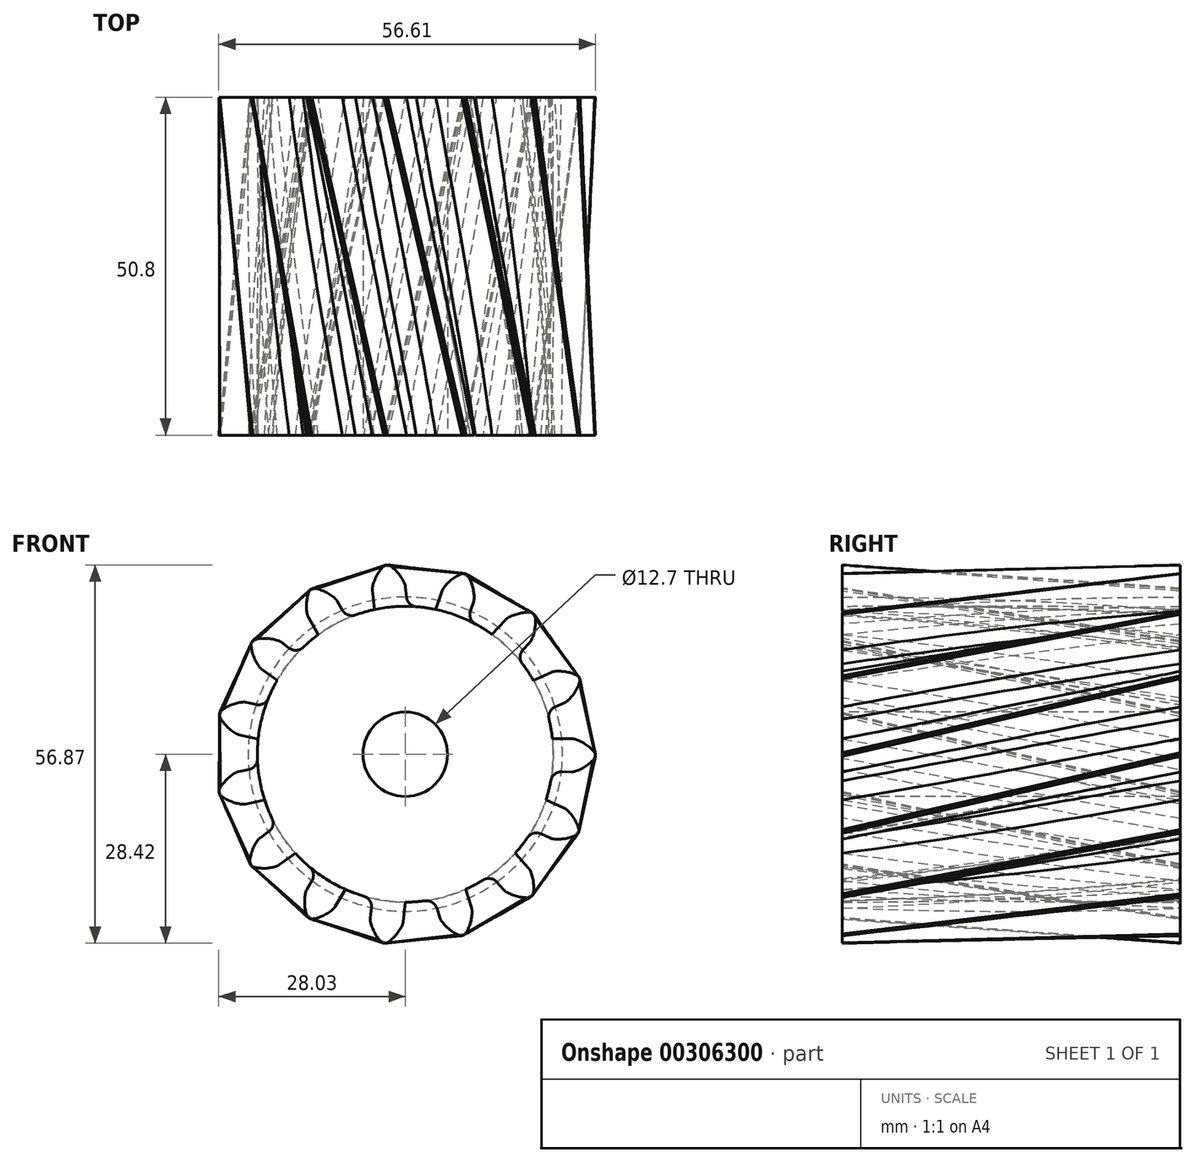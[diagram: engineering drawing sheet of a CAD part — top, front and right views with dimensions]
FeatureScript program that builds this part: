
annotation { "Feature Type Name" : "Feature", "Feature Type Description" : "" }
export const myFeature = defineFeature(function(context is Context, id is Id, definition is map)
    precondition{}
    {
        {
            var Q0;
            Q0=qCreatedBy(makeId("Front.planeOp"),FACE);
            var sketch = newSketch(context, id + "F0", { "sketchPlane" : qUnion([Q0])});
            skCircle(sketch, "E0", {"center": v(0, 0) * mm, "radius": 22.23 * mm});
            skArc(sketch, "E1.trimOffspring", {"start": v(-0.1, 25.65) * mm, "mid": v(-1.03, 27.16) * mm, "end": v(-2.34, 28.36) * mm});
            skLineSegment(sketch, "E2", {"start": v(0.02, 25.17) * mm, "end": v(0.31, 22.22) * mm});
            skLineSegment(sketch, "E3", {"start": v(-2.68, 28.45) * mm, "end": v(-2.8, 28.44) * mm});
            skLineSegment(sketch, "E4.MirrorCS", {"start": v(-4.93, 24.68) * mm, "end": v(-4.64, 21.73) * mm});
            skArc(sketch, "E5.MirrorCS", {"start": v(-4.9, 25.18) * mm, "mid": v(-4.29, 26.84) * mm, "end": v(-3.24, 28.27) * mm});
            skLineSegment(sketch, "E6.MirrorCS", {"start": v(-2.92, 28.42) * mm, "end": v(-2.8, 28.44) * mm});
            skPoint(sketch, "E7.visualSharp", {"position": v(0, 25.4) * mm});
            skArc(sketch, "E7.filletArc", {"start": v(0.02, 25.17) * mm, "mid": v(-0.02, 25.41) * mm, "end": v(-0.1, 25.65) * mm});
            skPoint(sketch, "E8.visualSharp", {"position": v(-4.96, 24.91) * mm});
            skArc(sketch, "E8.filletArc", {"start": v(-4.9, 25.18) * mm, "mid": v(-4.94, 24.93) * mm, "end": v(-4.93, 24.68) * mm});
            skPoint(sketch, "E9.visualSharp", {"position": v(-3.1, 28.4) * mm});
            skArc(sketch, "E9.filletArc", {"start": v(-2.92, 28.42) * mm, "mid": v(-3.1, 28.38) * mm, "end": v(-3.24, 28.27) * mm});
            skPoint(sketch, "E10.visualSharp", {"position": v(-2.5, 28.47) * mm});
            skArc(sketch, "E10.filletArc", {"start": v(-2.34, 28.36) * mm, "mid": v(-2.5, 28.43) * mm, "end": v(-2.68, 28.45) * mm});
            skSolve(sketch);
        }
        {
            var Q0;
            Q0=qCreatedBy(makeId("Front.planeOp"),FACE);
            cPlane(context, id + "F1", {"entities" : qUnion([Q0]), "cplaneType" : CPlaneType.OFFSET, "offset" : 50.8 * mm, "width" : 152.4 * mm, "height" : 152.4 * mm});
        }
        {
            var Q0;
            Q0=qCreatedBy(id+"F1.planeOp",FACE);
            var sketch = newSketch(context, id + "F2", { "sketchPlane" : qUnion([Q0])});
            skCircle(sketch, "E11.0", {"center": v(0, 0) * mm, "radius": 22.23 * mm});
            skArc(sketch, "E12.0.0", {"start": v(-3.24, 28.27) * mm, "mid": v(-4.29, 26.84) * mm, "end": v(-4.9, 25.18) * mm});
            skArc(sketch, "E12.0.1", {"start": v(-4.9, 25.18) * mm, "mid": v(-4.94, 24.93) * mm, "end": v(-4.93, 24.68) * mm});
            skLineSegment(sketch, "E12.0.2", {"start": v(-4.93, 24.68) * mm, "end": v(-4.64, 21.73) * mm});
            skArc(sketch, "E12.0.3", {"start": v(-4.64, 21.73) * mm, "mid": v(-2.18, 22.12) * mm, "end": v(0.31, 22.22) * mm});
            skLineSegment(sketch, "E12.0.4", {"start": v(0.31, 22.22) * mm, "end": v(0.02, 25.17) * mm});
            skArc(sketch, "E12.0.5", {"start": v(0.02, 25.17) * mm, "mid": v(-0.02, 25.41) * mm, "end": v(-0.1, 25.65) * mm});
            skArc(sketch, "E12.0.6", {"start": v(-0.1, 25.65) * mm, "mid": v(-1.03, 27.16) * mm, "end": v(-2.34, 28.36) * mm});
            skArc(sketch, "E12.0.7", {"start": v(-2.34, 28.36) * mm, "mid": v(-2.5, 28.43) * mm, "end": v(-2.68, 28.45) * mm});
            skLineSegment(sketch, "E12.0.8", {"start": v(-2.68, 28.45) * mm, "end": v(-2.8, 28.44) * mm});
            skLineSegment(sketch, "E12.0.9", {"start": v(-2.8, 28.44) * mm, "end": v(-2.92, 28.42) * mm});
            skArc(sketch, "E12.0.10", {"start": v(-2.92, 28.42) * mm, "mid": v(-3.1, 28.38) * mm, "end": v(-3.24, 28.27) * mm});
            skLineSegment(sketch, "E13.1.0", {"start": v(-8.75, 20.43) * mm, "end": v(-10.22, 23) * mm});
            skArc(sketch, "E13.1.1", {"start": v(-10.22, 23) * mm, "mid": v(-10.36, 23.2) * mm, "end": v(-10.53, 23.39) * mm});
            skArc(sketch, "E13.1.2", {"start": v(-10.53, 23.39) * mm, "mid": v(-11.99, 24.4) * mm, "end": v(-13.67, 24.96) * mm});
            skArc(sketch, "E13.1.3", {"start": v(-13.67, 24.96) * mm, "mid": v(-13.85, 24.96) * mm, "end": v(-14.02, 24.9) * mm});
            skLineSegment(sketch, "E13.1.4", {"start": v(-14.02, 24.9) * mm, "end": v(-14.12, 24.84) * mm});
            skLineSegment(sketch, "E13.1.5", {"start": v(-14.12, 24.84) * mm, "end": v(-14.23, 24.78) * mm});
            skArc(sketch, "E13.1.6", {"start": v(-14.23, 24.78) * mm, "mid": v(-14.37, 24.66) * mm, "end": v(-14.46, 24.51) * mm});
            skArc(sketch, "E13.1.7", {"start": v(-14.46, 24.51) * mm, "mid": v(-14.84, 22.78) * mm, "end": v(-14.72, 21) * mm});
            skArc(sketch, "E13.1.8", {"start": v(-14.72, 21) * mm, "mid": v(-14.65, 20.77) * mm, "end": v(-14.54, 20.54) * mm});
            skLineSegment(sketch, "E13.1.9", {"start": v(-14.54, 20.54) * mm, "end": v(-13.08, 17.97) * mm});
            skLineSegment(sketch, "E13.2.0", {"start": v(-16.3, 15.1) * mm, "end": v(-18.69, 16.86) * mm});
            skArc(sketch, "E13.2.1", {"start": v(-18.69, 16.86) * mm, "mid": v(-18.9, 16.99) * mm, "end": v(-19.13, 17.09) * mm});
            skArc(sketch, "E13.2.2", {"start": v(-19.13, 17.09) * mm, "mid": v(-20.88, 17.41) * mm, "end": v(-22.64, 17.24) * mm});
            skArc(sketch, "E13.2.3", {"start": v(-22.64, 17.24) * mm, "mid": v(-22.8, 17.17) * mm, "end": v(-22.93, 17.05) * mm});
            skLineSegment(sketch, "E13.2.4", {"start": v(-22.93, 17.05) * mm, "end": v(-23, 16.95) * mm});
            skLineSegment(sketch, "E13.2.5", {"start": v(-23, 16.95) * mm, "end": v(-23.08, 16.85) * mm});
            skArc(sketch, "E13.2.6", {"start": v(-23.08, 16.85) * mm, "mid": v(-23.16, 16.69) * mm, "end": v(-23.18, 16.51) * mm});
            skArc(sketch, "E13.2.7", {"start": v(-23.18, 16.51) * mm, "mid": v(-22.82, 14.77) * mm, "end": v(-22, 13.2) * mm});
            skArc(sketch, "E13.2.8", {"start": v(-22, 13.2) * mm, "mid": v(-21.83, 13.01) * mm, "end": v(-21.64, 12.85) * mm});
            skLineSegment(sketch, "E13.2.9", {"start": v(-21.64, 12.85) * mm, "end": v(-19.26, 11.1) * mm});
            skLineSegment(sketch, "E13.3.0", {"start": v(-21.04, 7.16) * mm, "end": v(-23.93, 7.8) * mm});
            skArc(sketch, "E13.3.1", {"start": v(-23.93, 7.8) * mm, "mid": v(-24.18, 7.83) * mm, "end": v(-24.42, 7.83) * mm});
            skArc(sketch, "E13.3.2", {"start": v(-24.42, 7.83) * mm, "mid": v(-26.15, 7.41) * mm, "end": v(-27.7, 6.54) * mm});
            skArc(sketch, "E13.3.3", {"start": v(-27.7, 6.54) * mm, "mid": v(-27.82, 6.4) * mm, "end": v(-27.88, 6.24) * mm});
            skLineSegment(sketch, "E13.3.4", {"start": v(-27.88, 6.24) * mm, "end": v(-27.9, 6.12) * mm});
            skLineSegment(sketch, "E13.3.5", {"start": v(-27.9, 6.12) * mm, "end": v(-27.94, 6) * mm});
            skArc(sketch, "E13.3.6", {"start": v(-27.94, 6) * mm, "mid": v(-27.94, 5.83) * mm, "end": v(-27.89, 5.66) * mm});
            skArc(sketch, "E13.3.7", {"start": v(-27.89, 5.66) * mm, "mid": v(-26.85, 4.22) * mm, "end": v(-25.46, 3.12) * mm});
            skArc(sketch, "E13.3.8", {"start": v(-25.46, 3.12) * mm, "mid": v(-25.23, 3) * mm, "end": v(-25, 2.94) * mm});
            skLineSegment(sketch, "E13.3.9", {"start": v(-25, 2.94) * mm, "end": v(-22.1, 2.3) * mm});
            skLineSegment(sketch, "E13.4.0", {"start": v(-22.13, -2.01) * mm, "end": v(-25.03, -2.6) * mm});
            skArc(sketch, "E13.4.1", {"start": v(-25.03, -2.6) * mm, "mid": v(-25.27, -2.68) * mm, "end": v(-25.5, -2.78) * mm});
            skArc(sketch, "E13.4.2", {"start": v(-25.5, -2.78) * mm, "mid": v(-26.9, -3.86) * mm, "end": v(-27.96, -5.3) * mm});
            skArc(sketch, "E13.4.3", {"start": v(-27.96, -5.3) * mm, "mid": v(-28.02, -5.46) * mm, "end": v(-28.01, -5.64) * mm});
            skLineSegment(sketch, "E13.4.4", {"start": v(-28.01, -5.64) * mm, "end": v(-27.99, -5.76) * mm});
            skLineSegment(sketch, "E13.4.5", {"start": v(-27.99, -5.76) * mm, "end": v(-27.96, -5.88) * mm});
            skArc(sketch, "E13.4.6", {"start": v(-27.96, -5.88) * mm, "mid": v(-27.9, -6.04) * mm, "end": v(-27.78, -6.17) * mm});
            skArc(sketch, "E13.4.7", {"start": v(-27.78, -6.17) * mm, "mid": v(-26.25, -7.07) * mm, "end": v(-24.53, -7.5) * mm});
            skArc(sketch, "E13.4.8", {"start": v(-24.53, -7.5) * mm, "mid": v(-24.28, -7.52) * mm, "end": v(-24.03, -7.49) * mm});
            skLineSegment(sketch, "E13.4.9", {"start": v(-24.03, -7.49) * mm, "end": v(-21.13, -6.89) * mm});
            skLineSegment(sketch, "E13.5.0", {"start": v(-19.4, -10.84) * mm, "end": v(-21.8, -12.56) * mm});
            skArc(sketch, "E13.5.1", {"start": v(-21.8, -12.56) * mm, "mid": v(-22, -12.72) * mm, "end": v(-22.16, -12.91) * mm});
            skArc(sketch, "E13.5.2", {"start": v(-22.16, -12.91) * mm, "mid": v(-23, -14.47) * mm, "end": v(-23.4, -16.2) * mm});
            skArc(sketch, "E13.5.3", {"start": v(-23.4, -16.2) * mm, "mid": v(-23.37, -16.38) * mm, "end": v(-23.3, -16.54) * mm});
            skLineSegment(sketch, "E13.5.4", {"start": v(-23.3, -16.54) * mm, "end": v(-23.23, -16.64) * mm});
            skLineSegment(sketch, "E13.5.5", {"start": v(-23.23, -16.64) * mm, "end": v(-23.15, -16.74) * mm});
            skArc(sketch, "E13.5.6", {"start": v(-23.15, -16.74) * mm, "mid": v(-23.03, -16.87) * mm, "end": v(-22.87, -16.94) * mm});
            skArc(sketch, "E13.5.7", {"start": v(-22.87, -16.94) * mm, "mid": v(-21.1, -17.14) * mm, "end": v(-19.35, -16.83) * mm});
            skArc(sketch, "E13.5.8", {"start": v(-19.35, -16.83) * mm, "mid": v(-19.12, -16.74) * mm, "end": v(-18.9, -16.61) * mm});
            skLineSegment(sketch, "E13.5.9", {"start": v(-18.9, -16.61) * mm, "end": v(-16.5, -14.89) * mm});
            skLineSegment(sketch, "E13.6.0", {"start": v(-13.32, -17.8) * mm, "end": v(-14.81, -20.35) * mm});
            skArc(sketch, "E13.6.1", {"start": v(-14.81, -20.35) * mm, "mid": v(-14.92, -20.57) * mm, "end": v(-15, -20.81) * mm});
            skArc(sketch, "E13.6.2", {"start": v(-15, -20.81) * mm, "mid": v(-15.13, -22.58) * mm, "end": v(-14.78, -24.32) * mm});
            skArc(sketch, "E13.6.3", {"start": v(-14.78, -24.32) * mm, "mid": v(-14.69, -24.47) * mm, "end": v(-14.55, -24.59) * mm});
            skLineSegment(sketch, "E13.6.4", {"start": v(-14.55, -24.59) * mm, "end": v(-14.45, -24.65) * mm});
            skLineSegment(sketch, "E13.6.5", {"start": v(-14.45, -24.65) * mm, "end": v(-14.34, -24.71) * mm});
            skArc(sketch, "E13.6.6", {"start": v(-14.34, -24.71) * mm, "mid": v(-14.18, -24.77) * mm, "end": v(-14, -24.78) * mm});
            skArc(sketch, "E13.6.7", {"start": v(-14, -24.78) * mm, "mid": v(-12.3, -24.24) * mm, "end": v(-10.83, -23.25) * mm});
            skArc(sketch, "E13.6.8", {"start": v(-10.83, -23.25) * mm, "mid": v(-10.66, -23.07) * mm, "end": v(-10.52, -22.87) * mm});
            skLineSegment(sketch, "E13.6.9", {"start": v(-10.52, -22.87) * mm, "end": v(-9.02, -20.31) * mm});
            skLineSegment(sketch, "E13.7.0", {"start": v(-4.93, -21.67) * mm, "end": v(-5.26, -24.61) * mm});
            skArc(sketch, "E13.7.1", {"start": v(-5.26, -24.61) * mm, "mid": v(-5.26, -24.86) * mm, "end": v(-5.23, -25.1) * mm});
            skArc(sketch, "E13.7.2", {"start": v(-5.23, -25.1) * mm, "mid": v(-4.64, -26.78) * mm, "end": v(-3.6, -28.23) * mm});
            skArc(sketch, "E13.7.3", {"start": v(-3.6, -28.23) * mm, "mid": v(-3.46, -28.33) * mm, "end": v(-3.3, -28.38) * mm});
            skLineSegment(sketch, "E13.7.4", {"start": v(-3.3, -28.38) * mm, "end": v(-3.17, -28.4) * mm});
            skLineSegment(sketch, "E13.7.5", {"start": v(-3.17, -28.4) * mm, "end": v(-3.05, -28.41) * mm});
            skArc(sketch, "E13.7.6", {"start": v(-3.05, -28.41) * mm, "mid": v(-2.87, -28.4) * mm, "end": v(-2.71, -28.33) * mm});
            skArc(sketch, "E13.7.7", {"start": v(-2.71, -28.33) * mm, "mid": v(-1.39, -27.15) * mm, "end": v(-0.44, -25.65) * mm});
            skArc(sketch, "E13.7.8", {"start": v(-0.44, -25.65) * mm, "mid": v(-0.35, -25.41) * mm, "end": v(-0.3, -25.17) * mm});
            skLineSegment(sketch, "E13.7.9", {"start": v(-0.3, -25.17) * mm, "end": v(0.02, -22.22) * mm});
            skLineSegment(sketch, "E13.8.0", {"start": v(4.31, -21.8) * mm, "end": v(5.21, -24.62) * mm});
            skArc(sketch, "E13.8.1", {"start": v(5.21, -24.62) * mm, "mid": v(5.3, -24.85) * mm, "end": v(5.43, -25.07) * mm});
            skArc(sketch, "E13.8.2", {"start": v(5.43, -25.07) * mm, "mid": v(6.66, -26.36) * mm, "end": v(8.19, -27.26) * mm});
            skArc(sketch, "E13.8.3", {"start": v(8.19, -27.26) * mm, "mid": v(8.36, -27.3) * mm, "end": v(8.53, -27.27) * mm});
            skLineSegment(sketch, "E13.8.4", {"start": v(8.53, -27.27) * mm, "end": v(8.65, -27.23) * mm});
            skLineSegment(sketch, "E13.8.5", {"start": v(8.65, -27.23) * mm, "end": v(8.77, -27.2) * mm});
            skArc(sketch, "E13.8.6", {"start": v(8.77, -27.2) * mm, "mid": v(8.93, -27.11) * mm, "end": v(9.04, -26.98) * mm});
            skArc(sketch, "E13.8.7", {"start": v(9.04, -26.98) * mm, "mid": v(9.78, -25.36) * mm, "end": v(10.03, -23.6) * mm});
            skArc(sketch, "E13.8.8", {"start": v(10.03, -23.6) * mm, "mid": v(10.01, -23.36) * mm, "end": v(9.96, -23.12) * mm});
            skLineSegment(sketch, "E13.8.9", {"start": v(9.96, -23.12) * mm, "end": v(9.06, -20.3) * mm});
            skLineSegment(sketch, "E13.9.0", {"start": v(12.8, -18.16) * mm, "end": v(14.78, -20.38) * mm});
            skArc(sketch, "E13.9.1", {"start": v(14.78, -20.38) * mm, "mid": v(14.95, -20.55) * mm, "end": v(15.16, -20.7) * mm});
            skArc(sketch, "E13.9.2", {"start": v(15.16, -20.7) * mm, "mid": v(16.8, -21.37) * mm, "end": v(18.56, -21.57) * mm});
            skArc(sketch, "E13.9.3", {"start": v(18.56, -21.57) * mm, "mid": v(18.74, -21.53) * mm, "end": v(18.89, -21.44) * mm});
            skLineSegment(sketch, "E13.9.4", {"start": v(18.89, -21.44) * mm, "end": v(18.98, -21.36) * mm});
            skLineSegment(sketch, "E13.9.5", {"start": v(18.98, -21.36) * mm, "end": v(19.07, -21.28) * mm});
            skArc(sketch, "E13.9.6", {"start": v(19.07, -21.28) * mm, "mid": v(19.18, -21.14) * mm, "end": v(19.24, -20.97) * mm});
            skArc(sketch, "E13.9.7", {"start": v(19.24, -20.97) * mm, "mid": v(19.25, -19.2) * mm, "end": v(18.77, -17.49) * mm});
            skArc(sketch, "E13.9.8", {"start": v(18.77, -17.49) * mm, "mid": v(18.65, -17.27) * mm, "end": v(18.5, -17.07) * mm});
            skLineSegment(sketch, "E13.9.9", {"start": v(18.5, -17.07) * mm, "end": v(16.53, -14.86) * mm});
            skLineSegment(sketch, "E13.10.0", {"start": v(19.09, -11.38) * mm, "end": v(21.79, -12.6) * mm});
            skArc(sketch, "E13.10.1", {"start": v(21.79, -12.6) * mm, "mid": v(22.02, -12.69) * mm, "end": v(22.26, -12.74) * mm});
            skArc(sketch, "E13.10.2", {"start": v(22.26, -12.74) * mm, "mid": v(24.04, -12.69) * mm, "end": v(25.73, -12.15) * mm});
            skArc(sketch, "E13.10.3", {"start": v(25.73, -12.15) * mm, "mid": v(25.88, -12.05) * mm, "end": v(25.98, -11.9) * mm});
            skLineSegment(sketch, "E13.10.4", {"start": v(25.98, -11.9) * mm, "end": v(26.03, -11.8) * mm});
            skLineSegment(sketch, "E13.10.5", {"start": v(26.03, -11.8) * mm, "end": v(26.08, -11.68) * mm});
            skArc(sketch, "E13.10.6", {"start": v(26.08, -11.68) * mm, "mid": v(26.12, -11.5) * mm, "end": v(26.1, -11.33) * mm});
            skArc(sketch, "E13.10.7", {"start": v(26.1, -11.33) * mm, "mid": v(25.4, -9.7) * mm, "end": v(24.25, -8.34) * mm});
            skArc(sketch, "E13.10.8", {"start": v(24.25, -8.34) * mm, "mid": v(24.06, -8.19) * mm, "end": v(23.84, -8.07) * mm});
            skLineSegment(sketch, "E13.10.9", {"start": v(23.84, -8.07) * mm, "end": v(21.14, -6.85) * mm});
            skLineSegment(sketch, "E13.11.0", {"start": v(22.07, -2.63) * mm, "end": v(25.03, -2.65) * mm});
            skArc(sketch, "E13.11.1", {"start": v(25.03, -2.65) * mm, "mid": v(25.28, -2.64) * mm, "end": v(25.52, -2.58) * mm});
            skArc(sketch, "E13.11.2", {"start": v(25.52, -2.58) * mm, "mid": v(27.12, -1.81) * mm, "end": v(28.45, -0.64) * mm});
            skArc(sketch, "E13.11.3", {"start": v(28.45, -0.64) * mm, "mid": v(28.54, -0.48) * mm, "end": v(28.57, -0.31) * mm});
            skLineSegment(sketch, "E13.11.4", {"start": v(28.57, -0.31) * mm, "end": v(28.57, -0.19) * mm});
            skLineSegment(sketch, "E13.11.5", {"start": v(28.57, -0.19) * mm, "end": v(28.57, -0.06) * mm});
            skArc(sketch, "E13.11.6", {"start": v(28.57, -0.06) * mm, "mid": v(28.54, 0.11) * mm, "end": v(28.46, 0.26) * mm});
            skArc(sketch, "E13.11.7", {"start": v(28.46, 0.26) * mm, "mid": v(27.14, 1.46) * mm, "end": v(25.55, 2.25) * mm});
            skArc(sketch, "E13.11.8", {"start": v(25.55, 2.25) * mm, "mid": v(25.3, 2.3) * mm, "end": v(25.06, 2.33) * mm});
            skLineSegment(sketch, "E13.11.9", {"start": v(25.06, 2.33) * mm, "end": v(22.1, 2.35) * mm});
            skLineSegment(sketch, "E13.12.0", {"start": v(21.23, 6.57) * mm, "end": v(23.94, 7.76) * mm});
            skArc(sketch, "E13.12.1", {"start": v(23.94, 7.76) * mm, "mid": v(24.16, 7.87) * mm, "end": v(24.36, 8.02) * mm});
            skArc(sketch, "E13.12.2", {"start": v(24.36, 8.02) * mm, "mid": v(25.52, 9.37) * mm, "end": v(26.25, 11) * mm});
            skArc(sketch, "E13.12.3", {"start": v(26.25, 11) * mm, "mid": v(26.27, 11.17) * mm, "end": v(26.23, 11.34) * mm});
            skLineSegment(sketch, "E13.12.4", {"start": v(26.23, 11.34) * mm, "end": v(26.18, 11.45) * mm});
            skLineSegment(sketch, "E13.12.5", {"start": v(26.18, 11.45) * mm, "end": v(26.13, 11.56) * mm});
            skArc(sketch, "E13.12.6", {"start": v(26.13, 11.56) * mm, "mid": v(26.03, 11.71) * mm, "end": v(25.89, 11.82) * mm});
            skArc(sketch, "E13.12.7", {"start": v(25.89, 11.82) * mm, "mid": v(24.2, 12.37) * mm, "end": v(22.43, 12.44) * mm});
            skArc(sketch, "E13.12.8", {"start": v(22.43, 12.44) * mm, "mid": v(22.18, 12.4) * mm, "end": v(21.95, 12.32) * mm});
            skLineSegment(sketch, "E13.12.9", {"start": v(21.95, 12.32) * mm, "end": v(19.24, 11.13) * mm});
            skLineSegment(sketch, "E13.13.0", {"start": v(16.72, 14.64) * mm, "end": v(18.72, 16.82) * mm});
            skArc(sketch, "E13.13.1", {"start": v(18.72, 16.82) * mm, "mid": v(18.87, 17.02) * mm, "end": v(19, 17.24) * mm});
            skArc(sketch, "E13.13.2", {"start": v(19, 17.24) * mm, "mid": v(19.5, 18.94) * mm, "end": v(19.51, 20.72) * mm});
            skArc(sketch, "E13.13.3", {"start": v(19.51, 20.72) * mm, "mid": v(19.46, 20.89) * mm, "end": v(19.35, 21.03) * mm});
            skLineSegment(sketch, "E13.13.4", {"start": v(19.35, 21.03) * mm, "end": v(19.26, 21.1) * mm});
            skLineSegment(sketch, "E13.13.5", {"start": v(19.26, 21.1) * mm, "end": v(19.17, 21.2) * mm});
            skArc(sketch, "E13.13.6", {"start": v(19.17, 21.2) * mm, "mid": v(19.02, 21.29) * mm, "end": v(18.85, 21.32) * mm});
            skArc(sketch, "E13.13.7", {"start": v(18.85, 21.32) * mm, "mid": v(17.08, 21.15) * mm, "end": v(15.43, 20.5) * mm});
            skArc(sketch, "E13.13.8", {"start": v(15.43, 20.5) * mm, "mid": v(15.22, 20.35) * mm, "end": v(15.04, 20.18) * mm});
            skLineSegment(sketch, "E13.13.9", {"start": v(15.04, 20.18) * mm, "end": v(13.05, 18) * mm});
            skLineSegment(sketch, "E13.14.0", {"start": v(9.32, 20.17) * mm, "end": v(10.26, 22.98) * mm});
            skArc(sketch, "E13.14.1", {"start": v(10.26, 22.98) * mm, "mid": v(10.32, 23.22) * mm, "end": v(10.34, 23.47) * mm});
            skArc(sketch, "E13.14.2", {"start": v(10.34, 23.47) * mm, "mid": v(10.1, 25.23) * mm, "end": v(9.4, 26.86) * mm});
            skArc(sketch, "E13.14.3", {"start": v(9.4, 26.86) * mm, "mid": v(9.28, 27) * mm, "end": v(9.12, 27.08) * mm});
            skLineSegment(sketch, "E13.14.4", {"start": v(9.12, 27.08) * mm, "end": v(9, 27.12) * mm});
            skLineSegment(sketch, "E13.14.5", {"start": v(9, 27.12) * mm, "end": v(8.9, 27.16) * mm});
            skArc(sketch, "E13.14.6", {"start": v(8.9, 27.16) * mm, "mid": v(8.72, 27.18) * mm, "end": v(8.54, 27.15) * mm});
            skArc(sketch, "E13.14.7", {"start": v(8.54, 27.15) * mm, "mid": v(7, 26.27) * mm, "end": v(5.76, 25) * mm});
            skArc(sketch, "E13.14.8", {"start": v(5.76, 25) * mm, "mid": v(5.63, 24.78) * mm, "end": v(5.53, 24.55) * mm});
            skLineSegment(sketch, "E13.14.9", {"start": v(5.53, 24.55) * mm, "end": v(4.6, 21.74) * mm});
            skSolve(sketch);
        }
        {
            var Q0;
            Q0=makeQuery(id+"F0.imprint","IMPRINT",FACE,{"disambiguationData":[TD([[makeQuery(id+"F0.imprint","IMPRINT",EDGE,{"derivedFrom":sQuery(id+"F0.wireOp",EDGE,"E1.trimOffspring")}),1.0]])]});
            var Q1;
            {var subQ0=sQuery(id+"F2.wireOp",EDGE,"E13.14.0");Q1=makeQuery(id+"F2.imprint","IMPRINT",FACE,{"disambiguationData":[TD([[makeQuery(id+"F2.imprint","IMPRINT",EDGE,{"derivedFrom":subQ0}),1.0]])]});}
            loft(context, id + "F3", {"sheetProfilesArray" : [{ "sheetProfileEntities" : qUnion([Q0]) }, { "sheetProfileEntities" : qUnion([Q1]) }]});
        }
        {
            var Q0;
            Q0=qCreatedBy(makeId("Front.planeOp"),FACE);
            var sketch = newSketch(context, id + "F4", { "sketchPlane" : qUnion([Q0])});
            skCircle(sketch, "E14", {"center": v(0, 0) * mm, "radius": 22.23 * mm});
            skSolve(sketch);
        }
        {
            var Q0;
            Q0=makeQuery(id+"F4.imprint","IMPRINT",FACE,{"disambiguationData":[TD([[makeQuery(id+"F4.imprint","IMPRINT",EDGE,{"derivedFrom":sQuery(id+"F4.wireOp",EDGE,"E14")}),1.0]])]});
            var Q1;
            {var subQ0=sQuery(id+"F2.wireOp",EDGE,"E13.14.0");Q1=makeQuery(id+"F3.opLoft","CAP_FACE",FACE,{"disambiguationData":[OSD([makeQuery(id+"F2.imprint","IMPRINT",FACE,{"disambiguationData":[TD([[makeQuery(id+"F2.imprint","IMPRINT",EDGE,{"derivedFrom":subQ0}),1.0]])]})])],"isStart":true});}
            extrude(context, id + "F5", {"entities" : qUnion([Q0]), "endBound" : BoundingType.UP_TO_SURFACE, "endBoundEntityFace" : qUnion([Q1]), "depth" : 25.4 * mm});
        }
        {
            var Q0;
            {var subQ0=sQuery(id+"F2.wireOp",EDGE,"E13.14.0");Q0=makeQuery(id+"F3.opLoft","SWEPT_BODY",BODY,{"disambiguationData":[OSD([makeQuery(id+"F0.imprint","IMPRINT",FACE,{"disambiguationData":[TD([[makeQuery(id+"F0.imprint","IMPRINT",EDGE,{"derivedFrom":sQuery(id+"F0.wireOp",EDGE,"E1.trimOffspring")}),1.0]])]}),makeQuery(id+"F2.imprint","IMPRINT",FACE,{"disambiguationData":[TD([[makeQuery(id+"F2.imprint","IMPRINT",EDGE,{"derivedFrom":subQ0}),1.0]])]})])]});}
            var Q1;
            Q1=makeQuery(id+"F5.opExtrude","CAP_EDGE",EDGE,{"disambiguationData":[OSD([sQuery(id+"F4.wireOp",EDGE,"E14")])],"isStart":false});
            circularPattern(context, id + "F6", {"entities" : qUnion([Q0]), "axis" : qUnion([Q1]), "angle" : 360 * degree, "instanceCount" : 15, "equalSpace" : true});
        }
        {
            var Q0;
            {var subQ0=sQuery(id+"F2.wireOp",EDGE,"E13.14.0");Q0=makeQuery(id+"F3.opLoft","SWEPT_BODY",BODY,{"disambiguationData":[OSD([makeQuery(id+"F0.imprint","IMPRINT",FACE,{"disambiguationData":[TD([[makeQuery(id+"F0.imprint","IMPRINT",EDGE,{"derivedFrom":sQuery(id+"F0.wireOp",EDGE,"E1.trimOffspring")}),1.0]])]}),makeQuery(id+"F2.imprint","IMPRINT",FACE,{"disambiguationData":[TD([[makeQuery(id+"F2.imprint","IMPRINT",EDGE,{"derivedFrom":subQ0}),1.0]])]})])]});}
            var Q1;
            Q1=makeQuery(id+"F5.opExtrude","SWEPT_BODY",BODY,{"disambiguationData":[OSD([sQuery(id+"F4.wireOp",EDGE,"E14")])]});
            var Q2;
            {var subQ0=sQuery(id+"F2.wireOp",EDGE,"E13.14.0");Q2=makeQuery(id+"F6.opPattern","COPY",BODY,{"derivedFrom":makeQuery(id+"F3.opLoft","SWEPT_BODY",BODY,{"disambiguationData":[OSD([makeQuery(id+"F0.imprint","IMPRINT",FACE,{"disambiguationData":[TD([[makeQuery(id+"F0.imprint","IMPRINT",EDGE,{"derivedFrom":sQuery(id+"F0.wireOp",EDGE,"E1.trimOffspring")}),1.0]])]}),makeQuery(id+"F2.imprint","IMPRINT",FACE,{"disambiguationData":[TD([[makeQuery(id+"F2.imprint","IMPRINT",EDGE,{"derivedFrom":subQ0}),1.0]])]})])]}),"instanceName":"14"});}
            var Q3;
            {var subQ0=sQuery(id+"F2.wireOp",EDGE,"E13.14.0");Q3=makeQuery(id+"F6.opPattern","COPY",BODY,{"derivedFrom":makeQuery(id+"F3.opLoft","SWEPT_BODY",BODY,{"disambiguationData":[OSD([makeQuery(id+"F0.imprint","IMPRINT",FACE,{"disambiguationData":[TD([[makeQuery(id+"F0.imprint","IMPRINT",EDGE,{"derivedFrom":sQuery(id+"F0.wireOp",EDGE,"E1.trimOffspring")}),1.0]])]}),makeQuery(id+"F2.imprint","IMPRINT",FACE,{"disambiguationData":[TD([[makeQuery(id+"F2.imprint","IMPRINT",EDGE,{"derivedFrom":subQ0}),1.0]])]})])]}),"instanceName":"13"});}
            var Q4;
            {var subQ0=sQuery(id+"F2.wireOp",EDGE,"E13.14.0");Q4=makeQuery(id+"F6.opPattern","COPY",BODY,{"derivedFrom":makeQuery(id+"F3.opLoft","SWEPT_BODY",BODY,{"disambiguationData":[OSD([makeQuery(id+"F0.imprint","IMPRINT",FACE,{"disambiguationData":[TD([[makeQuery(id+"F0.imprint","IMPRINT",EDGE,{"derivedFrom":sQuery(id+"F0.wireOp",EDGE,"E1.trimOffspring")}),1.0]])]}),makeQuery(id+"F2.imprint","IMPRINT",FACE,{"disambiguationData":[TD([[makeQuery(id+"F2.imprint","IMPRINT",EDGE,{"derivedFrom":subQ0}),1.0]])]})])]}),"instanceName":"12"});}
            var Q5;
            {var subQ0=sQuery(id+"F2.wireOp",EDGE,"E13.14.0");Q5=makeQuery(id+"F6.opPattern","COPY",BODY,{"derivedFrom":makeQuery(id+"F3.opLoft","SWEPT_BODY",BODY,{"disambiguationData":[OSD([makeQuery(id+"F0.imprint","IMPRINT",FACE,{"disambiguationData":[TD([[makeQuery(id+"F0.imprint","IMPRINT",EDGE,{"derivedFrom":sQuery(id+"F0.wireOp",EDGE,"E1.trimOffspring")}),1.0]])]}),makeQuery(id+"F2.imprint","IMPRINT",FACE,{"disambiguationData":[TD([[makeQuery(id+"F2.imprint","IMPRINT",EDGE,{"derivedFrom":subQ0}),1.0]])]})])]}),"instanceName":"10"});}
            var Q6;
            {var subQ0=sQuery(id+"F2.wireOp",EDGE,"E13.14.0");Q6=makeQuery(id+"F6.opPattern","COPY",BODY,{"derivedFrom":makeQuery(id+"F3.opLoft","SWEPT_BODY",BODY,{"disambiguationData":[OSD([makeQuery(id+"F0.imprint","IMPRINT",FACE,{"disambiguationData":[TD([[makeQuery(id+"F0.imprint","IMPRINT",EDGE,{"derivedFrom":sQuery(id+"F0.wireOp",EDGE,"E1.trimOffspring")}),1.0]])]}),makeQuery(id+"F2.imprint","IMPRINT",FACE,{"disambiguationData":[TD([[makeQuery(id+"F2.imprint","IMPRINT",EDGE,{"derivedFrom":subQ0}),1.0]])]})])]}),"instanceName":"9"});}
            var Q7;
            {var subQ0=sQuery(id+"F2.wireOp",EDGE,"E13.14.0");Q7=makeQuery(id+"F6.opPattern","COPY",BODY,{"derivedFrom":makeQuery(id+"F3.opLoft","SWEPT_BODY",BODY,{"disambiguationData":[OSD([makeQuery(id+"F0.imprint","IMPRINT",FACE,{"disambiguationData":[TD([[makeQuery(id+"F0.imprint","IMPRINT",EDGE,{"derivedFrom":sQuery(id+"F0.wireOp",EDGE,"E1.trimOffspring")}),1.0]])]}),makeQuery(id+"F2.imprint","IMPRINT",FACE,{"disambiguationData":[TD([[makeQuery(id+"F2.imprint","IMPRINT",EDGE,{"derivedFrom":subQ0}),1.0]])]})])]}),"instanceName":"8"});}
            var Q8;
            {var subQ0=sQuery(id+"F2.wireOp",EDGE,"E13.14.0");Q8=makeQuery(id+"F6.opPattern","COPY",BODY,{"derivedFrom":makeQuery(id+"F3.opLoft","SWEPT_BODY",BODY,{"disambiguationData":[OSD([makeQuery(id+"F0.imprint","IMPRINT",FACE,{"disambiguationData":[TD([[makeQuery(id+"F0.imprint","IMPRINT",EDGE,{"derivedFrom":sQuery(id+"F0.wireOp",EDGE,"E1.trimOffspring")}),1.0]])]}),makeQuery(id+"F2.imprint","IMPRINT",FACE,{"disambiguationData":[TD([[makeQuery(id+"F2.imprint","IMPRINT",EDGE,{"derivedFrom":subQ0}),1.0]])]})])]}),"instanceName":"7"});}
            var Q9;
            {var subQ0=sQuery(id+"F2.wireOp",EDGE,"E13.14.0");Q9=makeQuery(id+"F6.opPattern","COPY",BODY,{"derivedFrom":makeQuery(id+"F3.opLoft","SWEPT_BODY",BODY,{"disambiguationData":[OSD([makeQuery(id+"F0.imprint","IMPRINT",FACE,{"disambiguationData":[TD([[makeQuery(id+"F0.imprint","IMPRINT",EDGE,{"derivedFrom":sQuery(id+"F0.wireOp",EDGE,"E1.trimOffspring")}),1.0]])]}),makeQuery(id+"F2.imprint","IMPRINT",FACE,{"disambiguationData":[TD([[makeQuery(id+"F2.imprint","IMPRINT",EDGE,{"derivedFrom":subQ0}),1.0]])]})])]}),"instanceName":"6"});}
            var Q10;
            {var subQ0=sQuery(id+"F2.wireOp",EDGE,"E13.14.0");Q10=makeQuery(id+"F6.opPattern","COPY",BODY,{"derivedFrom":makeQuery(id+"F3.opLoft","SWEPT_BODY",BODY,{"disambiguationData":[OSD([makeQuery(id+"F0.imprint","IMPRINT",FACE,{"disambiguationData":[TD([[makeQuery(id+"F0.imprint","IMPRINT",EDGE,{"derivedFrom":sQuery(id+"F0.wireOp",EDGE,"E1.trimOffspring")}),1.0]])]}),makeQuery(id+"F2.imprint","IMPRINT",FACE,{"disambiguationData":[TD([[makeQuery(id+"F2.imprint","IMPRINT",EDGE,{"derivedFrom":subQ0}),1.0]])]})])]}),"instanceName":"5"});}
            var Q11;
            {var subQ0=sQuery(id+"F2.wireOp",EDGE,"E13.14.0");Q11=makeQuery(id+"F6.opPattern","COPY",BODY,{"derivedFrom":makeQuery(id+"F3.opLoft","SWEPT_BODY",BODY,{"disambiguationData":[OSD([makeQuery(id+"F0.imprint","IMPRINT",FACE,{"disambiguationData":[TD([[makeQuery(id+"F0.imprint","IMPRINT",EDGE,{"derivedFrom":sQuery(id+"F0.wireOp",EDGE,"E1.trimOffspring")}),1.0]])]}),makeQuery(id+"F2.imprint","IMPRINT",FACE,{"disambiguationData":[TD([[makeQuery(id+"F2.imprint","IMPRINT",EDGE,{"derivedFrom":subQ0}),1.0]])]})])]}),"instanceName":"4"});}
            var Q12;
            {var subQ0=sQuery(id+"F2.wireOp",EDGE,"E13.14.0");Q12=makeQuery(id+"F6.opPattern","COPY",BODY,{"derivedFrom":makeQuery(id+"F3.opLoft","SWEPT_BODY",BODY,{"disambiguationData":[OSD([makeQuery(id+"F0.imprint","IMPRINT",FACE,{"disambiguationData":[TD([[makeQuery(id+"F0.imprint","IMPRINT",EDGE,{"derivedFrom":sQuery(id+"F0.wireOp",EDGE,"E1.trimOffspring")}),1.0]])]}),makeQuery(id+"F2.imprint","IMPRINT",FACE,{"disambiguationData":[TD([[makeQuery(id+"F2.imprint","IMPRINT",EDGE,{"derivedFrom":subQ0}),1.0]])]})])]}),"instanceName":"3"});}
            var Q13;
            {var subQ0=sQuery(id+"F2.wireOp",EDGE,"E13.14.0");Q13=makeQuery(id+"F6.opPattern","COPY",BODY,{"derivedFrom":makeQuery(id+"F3.opLoft","SWEPT_BODY",BODY,{"disambiguationData":[OSD([makeQuery(id+"F0.imprint","IMPRINT",FACE,{"disambiguationData":[TD([[makeQuery(id+"F0.imprint","IMPRINT",EDGE,{"derivedFrom":sQuery(id+"F0.wireOp",EDGE,"E1.trimOffspring")}),1.0]])]}),makeQuery(id+"F2.imprint","IMPRINT",FACE,{"disambiguationData":[TD([[makeQuery(id+"F2.imprint","IMPRINT",EDGE,{"derivedFrom":subQ0}),1.0]])]})])]}),"instanceName":"2"});}
            var Q14;
            {var subQ0=sQuery(id+"F2.wireOp",EDGE,"E13.14.0");Q14=makeQuery(id+"F6.opPattern","COPY",BODY,{"derivedFrom":makeQuery(id+"F3.opLoft","SWEPT_BODY",BODY,{"disambiguationData":[OSD([makeQuery(id+"F0.imprint","IMPRINT",FACE,{"disambiguationData":[TD([[makeQuery(id+"F0.imprint","IMPRINT",EDGE,{"derivedFrom":sQuery(id+"F0.wireOp",EDGE,"E1.trimOffspring")}),1.0]])]}),makeQuery(id+"F2.imprint","IMPRINT",FACE,{"disambiguationData":[TD([[makeQuery(id+"F2.imprint","IMPRINT",EDGE,{"derivedFrom":subQ0}),1.0]])]})])]}),"instanceName":"1"});}
            var Q15;
            {var subQ0=sQuery(id+"F2.wireOp",EDGE,"E13.14.0");Q15=makeQuery(id+"F6.opPattern","COPY",BODY,{"derivedFrom":makeQuery(id+"F3.opLoft","SWEPT_BODY",BODY,{"disambiguationData":[OSD([makeQuery(id+"F0.imprint","IMPRINT",FACE,{"disambiguationData":[TD([[makeQuery(id+"F0.imprint","IMPRINT",EDGE,{"derivedFrom":sQuery(id+"F0.wireOp",EDGE,"E1.trimOffspring")}),1.0]])]}),makeQuery(id+"F2.imprint","IMPRINT",FACE,{"disambiguationData":[TD([[makeQuery(id+"F2.imprint","IMPRINT",EDGE,{"derivedFrom":subQ0}),1.0]])]})])]}),"instanceName":"11"});}
            booleanBodies(context, id + "F7", {"operationType" : BooleanOperationType.UNION, "tools" : qUnion([Q0, Q1, Q2, Q3, Q4, Q5, Q6, Q7, Q8, Q9, Q10, Q11, Q12, Q13, Q14, Q15])});
        }
        {
            var Q0;
            Q0=makeQuery(id+"F7.opBoolean","INTERSECT",EDGE,{"disambiguationData":[OD(0.0)],"derivedFrom":[makeQuery(id+"F5.opExtrude","SWEPT_FACE",FACE,{"disambiguationData":[OSD([sQuery(id+"F4.wireOp",EDGE,"E14")])]}),makeQuery(id+"F6.opPattern","COPY",FACE,{"derivedFrom":makeQuery(id+"F3.opLoft","SWEPT_FACE",FACE,{"disambiguationData":[OSD([sQuery(id+"F0.wireOp",EDGE,"E0"),sQuery(id+"F0.wireOp",EDGE,"E2"),sQuery(id+"F0.wireOp",EDGE,"E7.filletArc"),sQuery(id+"F2.wireOp",EDGE,"E11.0"),sQuery(id+"F2.wireOp",EDGE,"E13.14.0"),sQuery(id+"F2.wireOp",EDGE,"E13.14.1")])]}),"instanceName":"14"})]});
            var Q1;
            Q1=makeQuery(id+"F7.opBoolean","INTERSECT",EDGE,{"disambiguationData":[OD(0.0)],"derivedFrom":[makeQuery(id+"F5.opExtrude","SWEPT_FACE",FACE,{"disambiguationData":[OSD([sQuery(id+"F4.wireOp",EDGE,"E14")])]}),makeQuery(id+"F6.opPattern","COPY",FACE,{"derivedFrom":makeQuery(id+"F3.opLoft","SWEPT_FACE",FACE,{"disambiguationData":[OSD([sQuery(id+"F0.wireOp",EDGE,"E0"),sQuery(id+"F0.wireOp",EDGE,"E2"),sQuery(id+"F0.wireOp",EDGE,"E7.filletArc"),sQuery(id+"F2.wireOp",EDGE,"E11.0"),sQuery(id+"F2.wireOp",EDGE,"E13.14.0"),sQuery(id+"F2.wireOp",EDGE,"E13.14.1")])]}),"instanceName":"13"})]});
            var Q2;
            Q2=makeQuery(id+"F7.opBoolean","INTERSECT",EDGE,{"disambiguationData":[OD(0.0)],"derivedFrom":[makeQuery(id+"F5.opExtrude","SWEPT_FACE",FACE,{"disambiguationData":[OSD([sQuery(id+"F4.wireOp",EDGE,"E14")])]}),makeQuery(id+"F6.opPattern","COPY",FACE,{"derivedFrom":makeQuery(id+"F3.opLoft","SWEPT_FACE",FACE,{"disambiguationData":[OSD([sQuery(id+"F0.wireOp",EDGE,"E0"),sQuery(id+"F0.wireOp",EDGE,"E2"),sQuery(id+"F0.wireOp",EDGE,"E7.filletArc"),sQuery(id+"F2.wireOp",EDGE,"E11.0"),sQuery(id+"F2.wireOp",EDGE,"E13.14.0"),sQuery(id+"F2.wireOp",EDGE,"E13.14.1")])]}),"instanceName":"12"})]});
            var Q3;
            Q3=makeQuery(id+"F7.opBoolean","INTERSECT",EDGE,{"disambiguationData":[OD(0.0)],"derivedFrom":[makeQuery(id+"F5.opExtrude","SWEPT_FACE",FACE,{"disambiguationData":[OSD([sQuery(id+"F4.wireOp",EDGE,"E14")])]}),makeQuery(id+"F6.opPattern","COPY",FACE,{"derivedFrom":makeQuery(id+"F3.opLoft","SWEPT_FACE",FACE,{"disambiguationData":[OSD([sQuery(id+"F0.wireOp",EDGE,"E0"),sQuery(id+"F0.wireOp",EDGE,"E2"),sQuery(id+"F0.wireOp",EDGE,"E7.filletArc"),sQuery(id+"F2.wireOp",EDGE,"E11.0"),sQuery(id+"F2.wireOp",EDGE,"E13.14.0"),sQuery(id+"F2.wireOp",EDGE,"E13.14.1")])]}),"instanceName":"11"})]});
            var Q4;
            Q4=makeQuery(id+"F7.opBoolean","INTERSECT",EDGE,{"disambiguationData":[OD(0.0)],"derivedFrom":[makeQuery(id+"F5.opExtrude","SWEPT_FACE",FACE,{"disambiguationData":[OSD([sQuery(id+"F4.wireOp",EDGE,"E14")])]}),makeQuery(id+"F6.opPattern","COPY",FACE,{"derivedFrom":makeQuery(id+"F3.opLoft","SWEPT_FACE",FACE,{"disambiguationData":[OSD([sQuery(id+"F0.wireOp",EDGE,"E0"),sQuery(id+"F0.wireOp",EDGE,"E2"),sQuery(id+"F0.wireOp",EDGE,"E7.filletArc"),sQuery(id+"F2.wireOp",EDGE,"E11.0"),sQuery(id+"F2.wireOp",EDGE,"E13.14.0"),sQuery(id+"F2.wireOp",EDGE,"E13.14.1")])]}),"instanceName":"10"})]});
            var Q5;
            Q5=makeQuery(id+"F7.opBoolean","INTERSECT",EDGE,{"disambiguationData":[OD(0.0)],"derivedFrom":[makeQuery(id+"F5.opExtrude","SWEPT_FACE",FACE,{"disambiguationData":[OSD([sQuery(id+"F4.wireOp",EDGE,"E14")])]}),makeQuery(id+"F6.opPattern","COPY",FACE,{"derivedFrom":makeQuery(id+"F3.opLoft","SWEPT_FACE",FACE,{"disambiguationData":[OSD([sQuery(id+"F0.wireOp",EDGE,"E0"),sQuery(id+"F0.wireOp",EDGE,"E2"),sQuery(id+"F0.wireOp",EDGE,"E7.filletArc"),sQuery(id+"F2.wireOp",EDGE,"E11.0"),sQuery(id+"F2.wireOp",EDGE,"E13.14.0"),sQuery(id+"F2.wireOp",EDGE,"E13.14.1")])]}),"instanceName":"9"})]});
            var Q6;
            Q6=makeQuery(id+"F7.opBoolean","INTERSECT",EDGE,{"disambiguationData":[OD(0.0)],"derivedFrom":[makeQuery(id+"F5.opExtrude","SWEPT_FACE",FACE,{"disambiguationData":[OSD([sQuery(id+"F4.wireOp",EDGE,"E14")])]}),makeQuery(id+"F6.opPattern","COPY",FACE,{"derivedFrom":makeQuery(id+"F3.opLoft","SWEPT_FACE",FACE,{"disambiguationData":[OSD([sQuery(id+"F0.wireOp",EDGE,"E0"),sQuery(id+"F0.wireOp",EDGE,"E2"),sQuery(id+"F0.wireOp",EDGE,"E7.filletArc"),sQuery(id+"F2.wireOp",EDGE,"E11.0"),sQuery(id+"F2.wireOp",EDGE,"E13.14.0"),sQuery(id+"F2.wireOp",EDGE,"E13.14.1")])]}),"instanceName":"8"})]});
            var Q7;
            Q7=makeQuery(id+"F7.opBoolean","INTERSECT",EDGE,{"disambiguationData":[OD(0.0)],"derivedFrom":[makeQuery(id+"F5.opExtrude","SWEPT_FACE",FACE,{"disambiguationData":[OSD([sQuery(id+"F4.wireOp",EDGE,"E14")])]}),makeQuery(id+"F6.opPattern","COPY",FACE,{"derivedFrom":makeQuery(id+"F3.opLoft","SWEPT_FACE",FACE,{"disambiguationData":[OSD([sQuery(id+"F0.wireOp",EDGE,"E0"),sQuery(id+"F0.wireOp",EDGE,"E2"),sQuery(id+"F0.wireOp",EDGE,"E7.filletArc"),sQuery(id+"F2.wireOp",EDGE,"E11.0"),sQuery(id+"F2.wireOp",EDGE,"E13.14.0"),sQuery(id+"F2.wireOp",EDGE,"E13.14.1")])]}),"instanceName":"7"})]});
            var Q8;
            Q8=makeQuery(id+"F7.opBoolean","INTERSECT",EDGE,{"disambiguationData":[OD(0.0)],"derivedFrom":[makeQuery(id+"F5.opExtrude","SWEPT_FACE",FACE,{"disambiguationData":[OSD([sQuery(id+"F4.wireOp",EDGE,"E14")])]}),makeQuery(id+"F6.opPattern","COPY",FACE,{"derivedFrom":makeQuery(id+"F3.opLoft","SWEPT_FACE",FACE,{"disambiguationData":[OSD([sQuery(id+"F0.wireOp",EDGE,"E0"),sQuery(id+"F0.wireOp",EDGE,"E2"),sQuery(id+"F0.wireOp",EDGE,"E7.filletArc"),sQuery(id+"F2.wireOp",EDGE,"E11.0"),sQuery(id+"F2.wireOp",EDGE,"E13.14.0"),sQuery(id+"F2.wireOp",EDGE,"E13.14.1")])]}),"instanceName":"6"})]});
            var Q9;
            Q9=makeQuery(id+"F7.opBoolean","INTERSECT",EDGE,{"disambiguationData":[OD(0.0)],"derivedFrom":[makeQuery(id+"F5.opExtrude","SWEPT_FACE",FACE,{"disambiguationData":[OSD([sQuery(id+"F4.wireOp",EDGE,"E14")])]}),makeQuery(id+"F6.opPattern","COPY",FACE,{"derivedFrom":makeQuery(id+"F3.opLoft","SWEPT_FACE",FACE,{"disambiguationData":[OSD([sQuery(id+"F0.wireOp",EDGE,"E0"),sQuery(id+"F0.wireOp",EDGE,"E2"),sQuery(id+"F0.wireOp",EDGE,"E7.filletArc"),sQuery(id+"F2.wireOp",EDGE,"E11.0"),sQuery(id+"F2.wireOp",EDGE,"E13.14.0"),sQuery(id+"F2.wireOp",EDGE,"E13.14.1")])]}),"instanceName":"5"})]});
            var Q10;
            Q10=makeQuery(id+"F7.opBoolean","INTERSECT",EDGE,{"disambiguationData":[OD(0.0)],"derivedFrom":[makeQuery(id+"F5.opExtrude","SWEPT_FACE",FACE,{"disambiguationData":[OSD([sQuery(id+"F4.wireOp",EDGE,"E14")])]}),makeQuery(id+"F6.opPattern","COPY",FACE,{"derivedFrom":makeQuery(id+"F3.opLoft","SWEPT_FACE",FACE,{"disambiguationData":[OSD([sQuery(id+"F0.wireOp",EDGE,"E0"),sQuery(id+"F0.wireOp",EDGE,"E2"),sQuery(id+"F0.wireOp",EDGE,"E7.filletArc"),sQuery(id+"F2.wireOp",EDGE,"E11.0"),sQuery(id+"F2.wireOp",EDGE,"E13.14.0"),sQuery(id+"F2.wireOp",EDGE,"E13.14.1")])]}),"instanceName":"4"})]});
            var Q11;
            Q11=makeQuery(id+"F7.opBoolean","INTERSECT",EDGE,{"disambiguationData":[OD(0.0)],"derivedFrom":[makeQuery(id+"F5.opExtrude","SWEPT_FACE",FACE,{"disambiguationData":[OSD([sQuery(id+"F4.wireOp",EDGE,"E14")])]}),makeQuery(id+"F6.opPattern","COPY",FACE,{"derivedFrom":makeQuery(id+"F3.opLoft","SWEPT_FACE",FACE,{"disambiguationData":[OSD([sQuery(id+"F0.wireOp",EDGE,"E0"),sQuery(id+"F0.wireOp",EDGE,"E2"),sQuery(id+"F0.wireOp",EDGE,"E7.filletArc"),sQuery(id+"F2.wireOp",EDGE,"E11.0"),sQuery(id+"F2.wireOp",EDGE,"E13.14.0"),sQuery(id+"F2.wireOp",EDGE,"E13.14.1")])]}),"instanceName":"3"})]});
            var Q12;
            Q12=makeQuery(id+"F7.opBoolean","INTERSECT",EDGE,{"disambiguationData":[OD(0.0)],"derivedFrom":[makeQuery(id+"F5.opExtrude","SWEPT_FACE",FACE,{"disambiguationData":[OSD([sQuery(id+"F4.wireOp",EDGE,"E14")])]}),makeQuery(id+"F6.opPattern","COPY",FACE,{"derivedFrom":makeQuery(id+"F3.opLoft","SWEPT_FACE",FACE,{"disambiguationData":[OSD([sQuery(id+"F0.wireOp",EDGE,"E0"),sQuery(id+"F0.wireOp",EDGE,"E2"),sQuery(id+"F0.wireOp",EDGE,"E7.filletArc"),sQuery(id+"F2.wireOp",EDGE,"E11.0"),sQuery(id+"F2.wireOp",EDGE,"E13.14.0"),sQuery(id+"F2.wireOp",EDGE,"E13.14.1")])]}),"instanceName":"2"})]});
            var Q13;
            Q13=makeQuery(id+"F7.opBoolean","INTERSECT",EDGE,{"disambiguationData":[OD(0.0)],"derivedFrom":[makeQuery(id+"F5.opExtrude","SWEPT_FACE",FACE,{"disambiguationData":[OSD([sQuery(id+"F4.wireOp",EDGE,"E14")])]}),makeQuery(id+"F6.opPattern","COPY",FACE,{"derivedFrom":makeQuery(id+"F3.opLoft","SWEPT_FACE",FACE,{"disambiguationData":[OSD([sQuery(id+"F0.wireOp",EDGE,"E0"),sQuery(id+"F0.wireOp",EDGE,"E2"),sQuery(id+"F0.wireOp",EDGE,"E7.filletArc"),sQuery(id+"F2.wireOp",EDGE,"E11.0"),sQuery(id+"F2.wireOp",EDGE,"E13.14.0"),sQuery(id+"F2.wireOp",EDGE,"E13.14.1")])]}),"instanceName":"1"})]});
            var Q14;
            Q14=makeQuery(id+"F7.opBoolean","INTERSECT",EDGE,{"disambiguationData":[OD(0.0)],"derivedFrom":[makeQuery(id+"F3.opLoft","SWEPT_FACE",FACE,{"disambiguationData":[OSD([sQuery(id+"F0.wireOp",EDGE,"E0"),sQuery(id+"F0.wireOp",EDGE,"E2"),sQuery(id+"F0.wireOp",EDGE,"E7.filletArc"),sQuery(id+"F2.wireOp",EDGE,"E11.0"),sQuery(id+"F2.wireOp",EDGE,"E13.14.0"),sQuery(id+"F2.wireOp",EDGE,"E13.14.1")])]}),makeQuery(id+"F5.opExtrude","SWEPT_FACE",FACE,{"disambiguationData":[OSD([sQuery(id+"F4.wireOp",EDGE,"E14")])]})]});
            var Q15;
            Q15=makeQuery(id+"F7.opBoolean","INTERSECT",EDGE,{"disambiguationData":[OD(1.0)],"derivedFrom":[makeQuery(id+"F5.opExtrude","SWEPT_FACE",FACE,{"disambiguationData":[OSD([sQuery(id+"F4.wireOp",EDGE,"E14")])]}),makeQuery(id+"F6.opPattern","COPY",FACE,{"derivedFrom":makeQuery(id+"F3.opLoft","SWEPT_FACE",FACE,{"disambiguationData":[OSD([sQuery(id+"F0.wireOp",EDGE,"E0"),sQuery(id+"F0.wireOp",EDGE,"E2"),sQuery(id+"F0.wireOp",EDGE,"E7.filletArc"),sQuery(id+"F2.wireOp",EDGE,"E11.0"),sQuery(id+"F2.wireOp",EDGE,"E13.14.0"),sQuery(id+"F2.wireOp",EDGE,"E13.14.1")])]}),"instanceName":"14"})]});
            var Q16;
            Q16=makeQuery(id+"F7.opBoolean","INTERSECT",EDGE,{"disambiguationData":[OD(1.0)],"derivedFrom":[makeQuery(id+"F3.opLoft","SWEPT_FACE",FACE,{"disambiguationData":[OSD([sQuery(id+"F0.wireOp",EDGE,"E0"),sQuery(id+"F0.wireOp",EDGE,"E2"),sQuery(id+"F0.wireOp",EDGE,"E7.filletArc"),sQuery(id+"F2.wireOp",EDGE,"E11.0"),sQuery(id+"F2.wireOp",EDGE,"E13.14.0"),sQuery(id+"F2.wireOp",EDGE,"E13.14.1")])]}),makeQuery(id+"F5.opExtrude","SWEPT_FACE",FACE,{"disambiguationData":[OSD([sQuery(id+"F4.wireOp",EDGE,"E14")])]})]});
            var Q17;
            Q17=makeQuery(id+"F7.opBoolean","INTERSECT",EDGE,{"disambiguationData":[OD(1.0)],"derivedFrom":[makeQuery(id+"F5.opExtrude","SWEPT_FACE",FACE,{"disambiguationData":[OSD([sQuery(id+"F4.wireOp",EDGE,"E14")])]}),makeQuery(id+"F6.opPattern","COPY",FACE,{"derivedFrom":makeQuery(id+"F3.opLoft","SWEPT_FACE",FACE,{"disambiguationData":[OSD([sQuery(id+"F0.wireOp",EDGE,"E0"),sQuery(id+"F0.wireOp",EDGE,"E2"),sQuery(id+"F0.wireOp",EDGE,"E7.filletArc"),sQuery(id+"F2.wireOp",EDGE,"E11.0"),sQuery(id+"F2.wireOp",EDGE,"E13.14.0"),sQuery(id+"F2.wireOp",EDGE,"E13.14.1")])]}),"instanceName":"1"})]});
            var Q18;
            Q18=makeQuery(id+"F7.opBoolean","INTERSECT",EDGE,{"disambiguationData":[OD(1.0)],"derivedFrom":[makeQuery(id+"F5.opExtrude","SWEPT_FACE",FACE,{"disambiguationData":[OSD([sQuery(id+"F4.wireOp",EDGE,"E14")])]}),makeQuery(id+"F6.opPattern","COPY",FACE,{"derivedFrom":makeQuery(id+"F3.opLoft","SWEPT_FACE",FACE,{"disambiguationData":[OSD([sQuery(id+"F0.wireOp",EDGE,"E0"),sQuery(id+"F0.wireOp",EDGE,"E2"),sQuery(id+"F0.wireOp",EDGE,"E7.filletArc"),sQuery(id+"F2.wireOp",EDGE,"E11.0"),sQuery(id+"F2.wireOp",EDGE,"E13.14.0"),sQuery(id+"F2.wireOp",EDGE,"E13.14.1")])]}),"instanceName":"2"})]});
            var Q19;
            Q19=makeQuery(id+"F7.opBoolean","INTERSECT",EDGE,{"disambiguationData":[OD(1.0)],"derivedFrom":[makeQuery(id+"F5.opExtrude","SWEPT_FACE",FACE,{"disambiguationData":[OSD([sQuery(id+"F4.wireOp",EDGE,"E14")])]}),makeQuery(id+"F6.opPattern","COPY",FACE,{"derivedFrom":makeQuery(id+"F3.opLoft","SWEPT_FACE",FACE,{"disambiguationData":[OSD([sQuery(id+"F0.wireOp",EDGE,"E0"),sQuery(id+"F0.wireOp",EDGE,"E2"),sQuery(id+"F0.wireOp",EDGE,"E7.filletArc"),sQuery(id+"F2.wireOp",EDGE,"E11.0"),sQuery(id+"F2.wireOp",EDGE,"E13.14.0"),sQuery(id+"F2.wireOp",EDGE,"E13.14.1")])]}),"instanceName":"3"})]});
            var Q20;
            Q20=makeQuery(id+"F7.opBoolean","INTERSECT",EDGE,{"disambiguationData":[OD(1.0)],"derivedFrom":[makeQuery(id+"F5.opExtrude","SWEPT_FACE",FACE,{"disambiguationData":[OSD([sQuery(id+"F4.wireOp",EDGE,"E14")])]}),makeQuery(id+"F6.opPattern","COPY",FACE,{"derivedFrom":makeQuery(id+"F3.opLoft","SWEPT_FACE",FACE,{"disambiguationData":[OSD([sQuery(id+"F0.wireOp",EDGE,"E0"),sQuery(id+"F0.wireOp",EDGE,"E2"),sQuery(id+"F0.wireOp",EDGE,"E7.filletArc"),sQuery(id+"F2.wireOp",EDGE,"E11.0"),sQuery(id+"F2.wireOp",EDGE,"E13.14.0"),sQuery(id+"F2.wireOp",EDGE,"E13.14.1")])]}),"instanceName":"4"})]});
            var Q21;
            Q21=makeQuery(id+"F7.opBoolean","INTERSECT",EDGE,{"disambiguationData":[OD(1.0)],"derivedFrom":[makeQuery(id+"F5.opExtrude","SWEPT_FACE",FACE,{"disambiguationData":[OSD([sQuery(id+"F4.wireOp",EDGE,"E14")])]}),makeQuery(id+"F6.opPattern","COPY",FACE,{"derivedFrom":makeQuery(id+"F3.opLoft","SWEPT_FACE",FACE,{"disambiguationData":[OSD([sQuery(id+"F0.wireOp",EDGE,"E0"),sQuery(id+"F0.wireOp",EDGE,"E2"),sQuery(id+"F0.wireOp",EDGE,"E7.filletArc"),sQuery(id+"F2.wireOp",EDGE,"E11.0"),sQuery(id+"F2.wireOp",EDGE,"E13.14.0"),sQuery(id+"F2.wireOp",EDGE,"E13.14.1")])]}),"instanceName":"5"})]});
            var Q22;
            Q22=makeQuery(id+"F7.opBoolean","INTERSECT",EDGE,{"disambiguationData":[OD(1.0)],"derivedFrom":[makeQuery(id+"F5.opExtrude","SWEPT_FACE",FACE,{"disambiguationData":[OSD([sQuery(id+"F4.wireOp",EDGE,"E14")])]}),makeQuery(id+"F6.opPattern","COPY",FACE,{"derivedFrom":makeQuery(id+"F3.opLoft","SWEPT_FACE",FACE,{"disambiguationData":[OSD([sQuery(id+"F0.wireOp",EDGE,"E0"),sQuery(id+"F0.wireOp",EDGE,"E2"),sQuery(id+"F0.wireOp",EDGE,"E7.filletArc"),sQuery(id+"F2.wireOp",EDGE,"E11.0"),sQuery(id+"F2.wireOp",EDGE,"E13.14.0"),sQuery(id+"F2.wireOp",EDGE,"E13.14.1")])]}),"instanceName":"6"})]});
            var Q23;
            Q23=makeQuery(id+"F7.opBoolean","INTERSECT",EDGE,{"disambiguationData":[OD(1.0)],"derivedFrom":[makeQuery(id+"F5.opExtrude","SWEPT_FACE",FACE,{"disambiguationData":[OSD([sQuery(id+"F4.wireOp",EDGE,"E14")])]}),makeQuery(id+"F6.opPattern","COPY",FACE,{"derivedFrom":makeQuery(id+"F3.opLoft","SWEPT_FACE",FACE,{"disambiguationData":[OSD([sQuery(id+"F0.wireOp",EDGE,"E0"),sQuery(id+"F0.wireOp",EDGE,"E2"),sQuery(id+"F0.wireOp",EDGE,"E7.filletArc"),sQuery(id+"F2.wireOp",EDGE,"E11.0"),sQuery(id+"F2.wireOp",EDGE,"E13.14.0"),sQuery(id+"F2.wireOp",EDGE,"E13.14.1")])]}),"instanceName":"7"})]});
            var Q24;
            Q24=makeQuery(id+"F7.opBoolean","INTERSECT",EDGE,{"disambiguationData":[OD(1.0)],"derivedFrom":[makeQuery(id+"F5.opExtrude","SWEPT_FACE",FACE,{"disambiguationData":[OSD([sQuery(id+"F4.wireOp",EDGE,"E14")])]}),makeQuery(id+"F6.opPattern","COPY",FACE,{"derivedFrom":makeQuery(id+"F3.opLoft","SWEPT_FACE",FACE,{"disambiguationData":[OSD([sQuery(id+"F0.wireOp",EDGE,"E0"),sQuery(id+"F0.wireOp",EDGE,"E2"),sQuery(id+"F0.wireOp",EDGE,"E7.filletArc"),sQuery(id+"F2.wireOp",EDGE,"E11.0"),sQuery(id+"F2.wireOp",EDGE,"E13.14.0"),sQuery(id+"F2.wireOp",EDGE,"E13.14.1")])]}),"instanceName":"8"})]});
            var Q25;
            Q25=makeQuery(id+"F7.opBoolean","INTERSECT",EDGE,{"disambiguationData":[OD(1.0)],"derivedFrom":[makeQuery(id+"F5.opExtrude","SWEPT_FACE",FACE,{"disambiguationData":[OSD([sQuery(id+"F4.wireOp",EDGE,"E14")])]}),makeQuery(id+"F6.opPattern","COPY",FACE,{"derivedFrom":makeQuery(id+"F3.opLoft","SWEPT_FACE",FACE,{"disambiguationData":[OSD([sQuery(id+"F0.wireOp",EDGE,"E0"),sQuery(id+"F0.wireOp",EDGE,"E2"),sQuery(id+"F0.wireOp",EDGE,"E7.filletArc"),sQuery(id+"F2.wireOp",EDGE,"E11.0"),sQuery(id+"F2.wireOp",EDGE,"E13.14.0"),sQuery(id+"F2.wireOp",EDGE,"E13.14.1")])]}),"instanceName":"9"})]});
            var Q26;
            Q26=makeQuery(id+"F7.opBoolean","INTERSECT",EDGE,{"disambiguationData":[OD(1.0)],"derivedFrom":[makeQuery(id+"F5.opExtrude","SWEPT_FACE",FACE,{"disambiguationData":[OSD([sQuery(id+"F4.wireOp",EDGE,"E14")])]}),makeQuery(id+"F6.opPattern","COPY",FACE,{"derivedFrom":makeQuery(id+"F3.opLoft","SWEPT_FACE",FACE,{"disambiguationData":[OSD([sQuery(id+"F0.wireOp",EDGE,"E0"),sQuery(id+"F0.wireOp",EDGE,"E2"),sQuery(id+"F0.wireOp",EDGE,"E7.filletArc"),sQuery(id+"F2.wireOp",EDGE,"E11.0"),sQuery(id+"F2.wireOp",EDGE,"E13.14.0"),sQuery(id+"F2.wireOp",EDGE,"E13.14.1")])]}),"instanceName":"10"})]});
            var Q27;
            Q27=makeQuery(id+"F7.opBoolean","INTERSECT",EDGE,{"disambiguationData":[OD(1.0)],"derivedFrom":[makeQuery(id+"F5.opExtrude","SWEPT_FACE",FACE,{"disambiguationData":[OSD([sQuery(id+"F4.wireOp",EDGE,"E14")])]}),makeQuery(id+"F6.opPattern","COPY",FACE,{"derivedFrom":makeQuery(id+"F3.opLoft","SWEPT_FACE",FACE,{"disambiguationData":[OSD([sQuery(id+"F0.wireOp",EDGE,"E0"),sQuery(id+"F0.wireOp",EDGE,"E2"),sQuery(id+"F0.wireOp",EDGE,"E7.filletArc"),sQuery(id+"F2.wireOp",EDGE,"E11.0"),sQuery(id+"F2.wireOp",EDGE,"E13.14.0"),sQuery(id+"F2.wireOp",EDGE,"E13.14.1")])]}),"instanceName":"11"})]});
            var Q28;
            Q28=makeQuery(id+"F7.opBoolean","INTERSECT",EDGE,{"disambiguationData":[OD(1.0)],"derivedFrom":[makeQuery(id+"F5.opExtrude","SWEPT_FACE",FACE,{"disambiguationData":[OSD([sQuery(id+"F4.wireOp",EDGE,"E14")])]}),makeQuery(id+"F6.opPattern","COPY",FACE,{"derivedFrom":makeQuery(id+"F3.opLoft","SWEPT_FACE",FACE,{"disambiguationData":[OSD([sQuery(id+"F0.wireOp",EDGE,"E0"),sQuery(id+"F0.wireOp",EDGE,"E2"),sQuery(id+"F0.wireOp",EDGE,"E7.filletArc"),sQuery(id+"F2.wireOp",EDGE,"E11.0"),sQuery(id+"F2.wireOp",EDGE,"E13.14.0"),sQuery(id+"F2.wireOp",EDGE,"E13.14.1")])]}),"instanceName":"12"})]});
            var Q29;
            Q29=makeQuery(id+"F7.opBoolean","INTERSECT",EDGE,{"disambiguationData":[OD(1.0)],"derivedFrom":[makeQuery(id+"F5.opExtrude","SWEPT_FACE",FACE,{"disambiguationData":[OSD([sQuery(id+"F4.wireOp",EDGE,"E14")])]}),makeQuery(id+"F6.opPattern","COPY",FACE,{"derivedFrom":makeQuery(id+"F3.opLoft","SWEPT_FACE",FACE,{"disambiguationData":[OSD([sQuery(id+"F0.wireOp",EDGE,"E0"),sQuery(id+"F0.wireOp",EDGE,"E2"),sQuery(id+"F0.wireOp",EDGE,"E7.filletArc"),sQuery(id+"F2.wireOp",EDGE,"E11.0"),sQuery(id+"F2.wireOp",EDGE,"E13.14.0"),sQuery(id+"F2.wireOp",EDGE,"E13.14.1")])]}),"instanceName":"13"})]});
            fillet(context, id + "F8", {"entities" : qUnion([Q0, Q1, Q2, Q3, Q4, Q5, Q6, Q7, Q8, Q9, Q10, Q11, Q12, Q13, Q14, Q15, Q16, Q17, Q18, Q19, Q20, Q21, Q22, Q23, Q24, Q25, Q26, Q27, Q28, Q29]), "radius" : 1.6 * mm, "tangentPropagation" : true, "allowEdgeOverflow" : false});
        }
        {
            var Q0;
            {var subQ0=sQuery(id+"F2.wireOp",EDGE,"E13.14.0");var subQ3=makeQuery(id+"F3.opLoft","CAP_FACE",FACE,{"disambiguationData":[OSD([makeQuery(id+"F2.imprint","IMPRINT",FACE,{"disambiguationData":[TD([[makeQuery(id+"F2.imprint","IMPRINT",EDGE,{"derivedFrom":subQ0}),1.0]])]})])],"isStart":true});Q0=makeQuery(id+"F7.opBoolean","MERGE",FACE,{"derivedFrom":[subQ3,makeQuery(id+"F5.opExtrude","CAP_FACE",FACE,{"disambiguationData":[OSD([sQuery(id+"F4.wireOp",EDGE,"E14")])],"isStart":false}),makeQuery(id+"F6.opPattern","COPY",FACE,{"derivedFrom":subQ3,"instanceName":"1"}),makeQuery(id+"F6.opPattern","COPY",FACE,{"derivedFrom":subQ3,"instanceName":"2"}),makeQuery(id+"F6.opPattern","COPY",FACE,{"derivedFrom":subQ3,"instanceName":"3"}),makeQuery(id+"F6.opPattern","COPY",FACE,{"derivedFrom":subQ3,"instanceName":"4"}),makeQuery(id+"F6.opPattern","COPY",FACE,{"derivedFrom":subQ3,"instanceName":"5"}),makeQuery(id+"F6.opPattern","COPY",FACE,{"derivedFrom":subQ3,"instanceName":"6"}),makeQuery(id+"F6.opPattern","COPY",FACE,{"derivedFrom":subQ3,"instanceName":"7"}),makeQuery(id+"F6.opPattern","COPY",FACE,{"derivedFrom":subQ3,"instanceName":"8"}),makeQuery(id+"F6.opPattern","COPY",FACE,{"derivedFrom":subQ3,"instanceName":"9"}),makeQuery(id+"F6.opPattern","COPY",FACE,{"derivedFrom":subQ3,"instanceName":"10"}),makeQuery(id+"F6.opPattern","COPY",FACE,{"derivedFrom":subQ3,"instanceName":"11"}),makeQuery(id+"F6.opPattern","COPY",FACE,{"derivedFrom":subQ3,"instanceName":"12"}),makeQuery(id+"F6.opPattern","COPY",FACE,{"derivedFrom":subQ3,"instanceName":"13"}),makeQuery(id+"F6.opPattern","COPY",FACE,{"derivedFrom":subQ3,"instanceName":"14"})]});}
            var sketch = newSketch(context, id + "F9", { "sketchPlane" : qUnion([Q0])});
            skPoint(sketch, "E15", {"position": v(0, 0) * mm});
            skSolve(sketch);
        }
        {
            var Q0;
            Q0=sQuery(id+"F9.wireOp",VERTEX,"E15");
            var Q1;
            {var subQ0=sQuery(id+"F2.wireOp",EDGE,"E13.14.0");Q1=makeQuery(id+"F3.opLoft","SWEPT_BODY",BODY,{"disambiguationData":[OSD([makeQuery(id+"F0.imprint","IMPRINT",FACE,{"disambiguationData":[TD([[makeQuery(id+"F0.imprint","IMPRINT",EDGE,{"derivedFrom":sQuery(id+"F0.wireOp",EDGE,"E1.trimOffspring")}),1.0]])]}),makeQuery(id+"F2.imprint","IMPRINT",FACE,{"disambiguationData":[TD([[makeQuery(id+"F2.imprint","IMPRINT",EDGE,{"derivedFrom":subQ0}),1.0]])]})])]});}
            hole(context, id + "F10", {"style" : HoleStyle.SIMPLE, "endStyle" : HoleEndStyle.THROUGH, "holeDiameter" : 12.7 * mm, "tappedDepth" : 12.7 * mm, "tapClearance" : 3, "locations" : qUnion([Q0]), "scope" : qUnion([Q1])});
        }
    });
